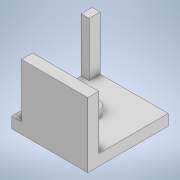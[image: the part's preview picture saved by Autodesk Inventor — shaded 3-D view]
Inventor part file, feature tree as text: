
AUTODESK INVENTOR PART (.ipt)
format: ipt  version: 2020 (Build 240168000, 168)  size: 159,232 bytes
history: native  units: in
note: dims shown in document units (in); Inventor stores cm internally (conversion verified against a paired STEP export)
features: extrude x6, sketch x6, chamfer x1
ambient origin geometry x8: Origin, YZ Plane, XZ Plane, XY Plane, X Axis, Y Axis, Z Axis, Center Point
bodies: Solid1 (feature_tree)
feature tree (13):
  extrude  "Extrusion1"  Depth=1.4331in
  extrude  "Extrusion2"  Depth=1.1811in
  extrude  "Extrusion3"  Depth=1.1811in
  extrude  "Extrusion4"  Depth=0.9606in TaperAngle=0.0deg
  extrude  "Extrusion5"  Depth=0.1969in
  chamfer  "Chamfer1"  Distance=0.1969in
  extrude  "Extrusion6"  Depth=1.3543in
  sketch  "Sketch1"  dims[d0=2.3937in d1=1.4331in]
  sketch  "Sketch2"  dims[d2=0.1969in d3=0.0in d4=1.1811in]
  sketch  "Sketch3"  dims[d5=0.1969in d6=1.1811in]
  sketch  "Sketch4"  dims[d7=0.1969in d8=0.9606in d9=0.0in]
  sketch  "Sketch5"  dims[d10=0.3406in d11=0.3406in d12=0.1969in d13=0.0in]
  sketch  "Sketch6"  dims[d14=0.1575in d15=0.1575in d16=0.5906in d17=0.0in d18=0.2362in d19=0.2362in d20=0.1181in d21=0.0in d22=0.0591in d23=0.0787in d24=45.0deg d26=1.3543in d27=1.9685in d28=0.0in d29=0.0197in d30=0.0344in]
